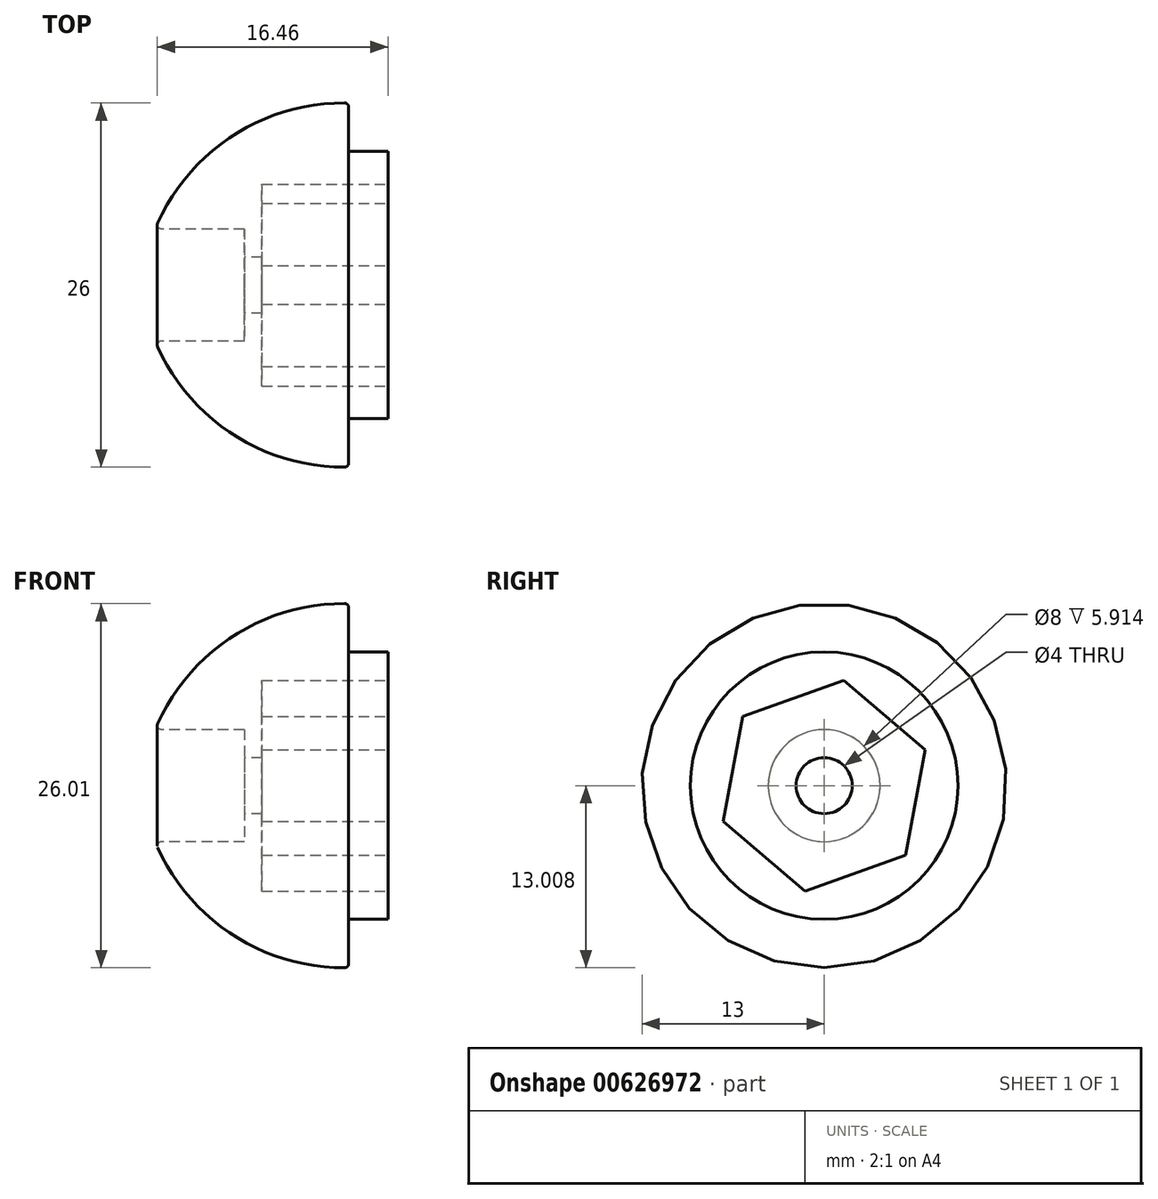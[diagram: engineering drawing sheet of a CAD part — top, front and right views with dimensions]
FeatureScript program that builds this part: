
annotation { "Feature Type Name" : "Feature", "Feature Type Description" : "" }
export const myFeature = defineFeature(function(context is Context, id is Id, definition is map)
    precondition{}
    {
        {
            var Q0;
            Q0=qCreatedBy(makeId("Front.planeOp"),FACE);
            var sketch = newSketch(context, id + "F0", { "sketchPlane" : qUnion([Q0])});
            skLineSegment(sketch, "E0", {"start": v(-56.23, 54.65) * mm, "end": v(-49.86, 54.65) * mm});
            skLineSegment(sketch, "E1", {"start": v(-49.86, 54.65) * mm, "end": v(-49.86, 52.65) * mm});
            skLineSegment(sketch, "E2", {"start": v(-49.86, 52.65) * mm, "end": v(-48.61, 52.65) * mm});
            skLineSegment(sketch, "E3", {"start": v(-48.61, 52.65) * mm, "end": v(-48.61, 54.3) * mm});
            skLineSegment(sketch, "E4", {"start": v(-48.61, 54.3) * mm, "end": v(-39.61, 54.3) * mm});
            skLineSegment(sketch, "E5", {"start": v(-39.61, 54.3) * mm, "end": v(-39.61, 60.2) * mm});
            skLineSegment(sketch, "E6", {"start": v(-39.61, 60.2) * mm, "end": v(-42.41, 60.2) * mm});
            skLineSegment(sketch, "E7", {"start": v(-42.41, 60.2) * mm, "end": v(-42.41, 63.65) * mm});
            skArc(sketch, "E8", {"start": v(-42.41, 63.65) * mm, "mid": v(-50.72, 61.3) * mm, "end": v(-56.23, 54.65) * mm});
            skLineSegment(sketch, "E9", {"start": v(-58.62, 50.65) * mm, "end": v(-33.61, 50.65) * mm, "construction": true});
            skSolve(sketch);
        }
        {
            var Q0;
            Q0=makeQuery(id+"F0.imprint","IMPRINT",FACE,{"disambiguationData":[TD([[makeQuery(id+"F0.imprint","IMPRINT",EDGE,{"derivedFrom":sQuery(id+"F0.wireOp",EDGE,"E0")}),1.0]])]});
            var Q1;
            Q1=sQuery(id+"F0.wireOp",EDGE,"E9");
            revolve(context, id + "F1", {"entities" : qUnion([Q0]), "axis" : qUnion([Q1]), "revolveType" : RevolveType.FULL});
        }
        {
            var Q0;
            Q0=makeQuery(id+"F1.opRevolve","SWEPT_FACE",FACE,{"disambiguationData":[OSD([sQuery(id+"F0.wireOp",EDGE,"E5")])]});
            var sketch = newSketch(context, id + "F2", { "sketchPlane" : qUnion([Q0])});
            skCircle(sketch, "E10.cCircle", {"center": v(0, 50.65) * mm, "radius": 7.65 * mm, "construction": true});
            skLineSegment(sketch, "E10.0", {"start": v(7.2, 53.21) * mm, "end": v(5.83, 45.69) * mm});
            skLineSegment(sketch, "E10.1", {"start": v(5.83, 45.69) * mm, "end": v(-1.38, 43.12) * mm});
            skLineSegment(sketch, "E10.2", {"start": v(-1.38, 43.12) * mm, "end": v(-7.2, 48.08) * mm});
            skLineSegment(sketch, "E10.3", {"start": v(-7.2, 48.08) * mm, "end": v(-5.83, 55.6) * mm});
            skLineSegment(sketch, "E10.4", {"start": v(-5.83, 55.6) * mm, "end": v(1.38, 58.17) * mm});
            skLineSegment(sketch, "E10.5", {"start": v(1.38, 58.17) * mm, "end": v(7.2, 53.21) * mm});
            skSolve(sketch);
        }
        {
            var Q0;
            Q0=makeQuery(id+"F2.imprint","IMPRINT",FACE,{"disambiguationData":[TD([[makeQuery(id+"F2.imprint","IMPRINT",EDGE,{"derivedFrom":sQuery(id+"F2.wireOp",EDGE,"E10.0")}),-1.0]])]});
            extrude(context, id + "F3", {"entities" : qUnion([Q0]), "operationType" : NewBodyOperationType.REMOVE, "oppositeDirection" : true, "depth" : 9 * mm, "offsetDistance" : 25 * mm});
        }
        {
            var Q0;
            Q0=makeQuery(id+"F1.opRevolve","SWEPT_EDGE",EDGE,{"disambiguationData":[OSD([sQuery(id+"F0.wireOp",EDGE,"E0"),sQuery(id+"F0.wireOp",EDGE,"E8")])]});
            var Q1;
            Q1=makeQuery(id+"F1.opRevolve","SWEPT_FACE",FACE,{"disambiguationData":[OSD([sQuery(id+"F0.wireOp",EDGE,"E8")])]});
            fillet(context, id + "F4", {"entities" : qUnion([Q0, Q1]), "radius" : 0.3 * mm, "tangentPropagation" : true, "allowEdgeOverflow" : false});
        }
    });
